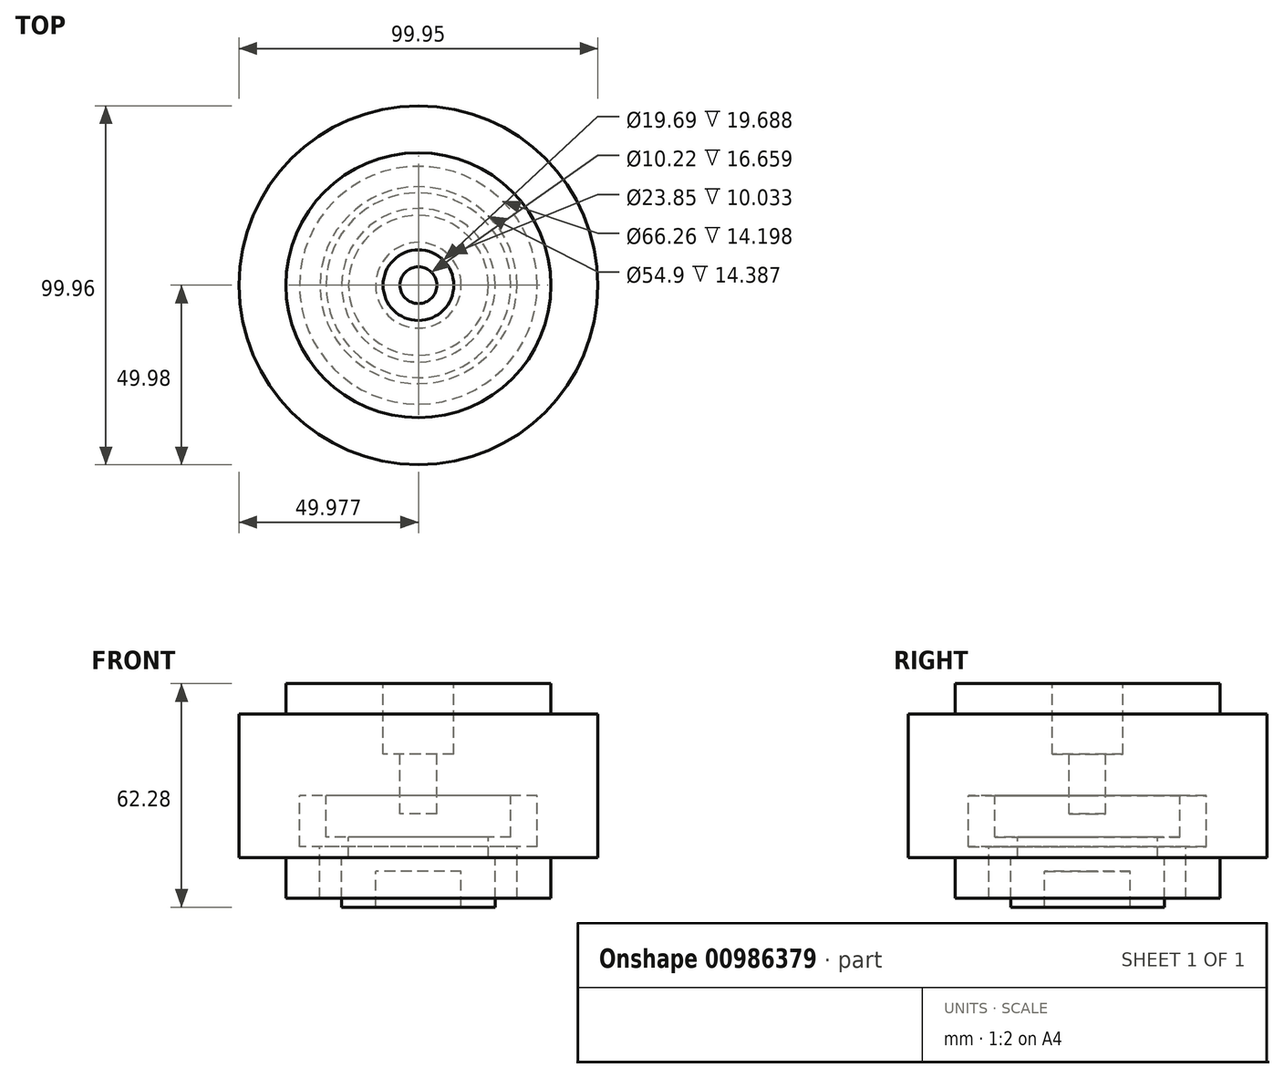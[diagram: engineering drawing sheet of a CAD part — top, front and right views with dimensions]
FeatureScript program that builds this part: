
annotation { "Feature Type Name" : "Feature", "Feature Type Description" : "" }
export const myFeature = defineFeature(function(context is Context, id is Id, definition is map)
    precondition{}
    {
        {
            var Q0;
            Q0=qCreatedBy(makeId("Front.planeOp"),FACE);
            var sketch = newSketch(context, id + "F0", { "sketchPlane" : qUnion([Q0])});
            skLineSegment(sketch, "E0.bottom", {"start": v(14.67, 16) * mm, "end": v(41.74, 16) * mm});
            skLineSegment(sketch, "E0.top", {"start": v(30.57, -15.24) * mm, "end": v(37.96, -15.24) * mm});
            skLineSegment(sketch, "E0.left", {"start": v(14.67, 16) * mm, "end": v(14.67, -3.7) * mm});
            skLineSegment(sketch, "E0.right", {"start": v(41.74, 16) * mm, "end": v(41.74, 7.48) * mm});
            skLineSegment(sketch, "E1.bottom", {"start": v(9.94, -3.7) * mm, "end": v(14.67, -3.7) * mm});
            skLineSegment(sketch, "E1.top", {"start": v(24.33, -26.79) * mm, "end": v(30.57, -26.79) * mm});
            skLineSegment(sketch, "E1.left", {"start": v(9.94, -3.7) * mm, "end": v(9.94, -20.35) * mm});
            skLineSegment(sketch, "E1.right", {"start": v(30.57, -15.24) * mm, "end": v(30.57, -26.79) * mm});
            skLineSegment(sketch, "E2.bottom", {"start": v(4.83, -20.35) * mm, "end": v(9.94, -20.35) * mm});
            skLineSegment(sketch, "E2.top", {"start": v(4.83, -36.25) * mm, "end": v(16.75, -36.25) * mm});
            skLineSegment(sketch, "E2.left", {"start": v(4.83, -20.35) * mm, "end": v(4.83, -36.25) * mm});
            skLineSegment(sketch, "E2.right", {"start": v(24.33, -26.79) * mm, "end": v(24.33, -32.47) * mm});
            skLineSegment(sketch, "E3.bottom", {"start": v(54.8, 7.48) * mm, "end": v(41.74, 7.48) * mm});
            skLineSegment(sketch, "E3.top", {"start": v(54.8, -32.47) * mm, "end": v(41.74, -32.47) * mm});
            skLineSegment(sketch, "E3.left", {"start": v(54.8, 7.48) * mm, "end": v(54.8, -32.47) * mm});
            skLineSegment(sketch, "E3.right", {"start": v(37.96, -15.24) * mm, "end": v(37.96, -29.44) * mm});
            skLineSegment(sketch, "E4.bottom", {"start": v(37.96, -29.44) * mm, "end": v(32.28, -29.44) * mm});
            skLineSegment(sketch, "E4.top", {"start": v(41.74, -43.82) * mm, "end": v(32.28, -43.82) * mm});
            skLineSegment(sketch, "E4.left", {"start": v(41.74, -32.47) * mm, "end": v(41.74, -43.82) * mm});
            skLineSegment(sketch, "E4.right", {"start": v(32.28, -29.44) * mm, "end": v(32.28, -43.82) * mm});
            skLineSegment(sketch, "E5.bottom", {"start": v(24.33, -32.47) * mm, "end": v(26.22, -32.47) * mm});
            skLineSegment(sketch, "E5.top", {"start": v(16.75, -46.28) * mm, "end": v(26.22, -46.28) * mm});
            skLineSegment(sketch, "E5.left", {"start": v(16.75, -36.25) * mm, "end": v(16.75, -46.28) * mm});
            skLineSegment(sketch, "E5.right", {"start": v(26.22, -32.47) * mm, "end": v(26.22, -46.28) * mm});
            skPoint(sketch, "E6.orphan", {"position": v(16.75, -32.47) * mm});
            skPoint(sketch, "E7.orphan", {"position": v(37.96, -32.47) * mm});
            skPoint(sketch, "E8.orphan", {"position": v(41.74, -29.44) * mm});
            skPoint(sketch, "E9.orphan", {"position": v(41.74, -15.24) * mm});
            skSolve(sketch);
        }
        {
            var Q0;
            Q0=makeQuery(id+"F0.imprint","IMPRINT",FACE,{"disambiguationData":[TD([[makeQuery(id+"F0.imprint","IMPRINT",EDGE,{"derivedFrom":sQuery(id+"F0.wireOp",EDGE,"E0.bottom")}),-1.0]])]});
            var Q1;
            Q1=sQuery(id+"F0.wireOp",EDGE,"E2.left");
            revolve(context, id + "F1", {"surfaceOperationType" : NewSurfaceOperationType.NEW, "entities" : qUnion([Q0]), "axis" : qUnion([Q1]), "revolveType" : RevolveType.FULL});
        }
    });
